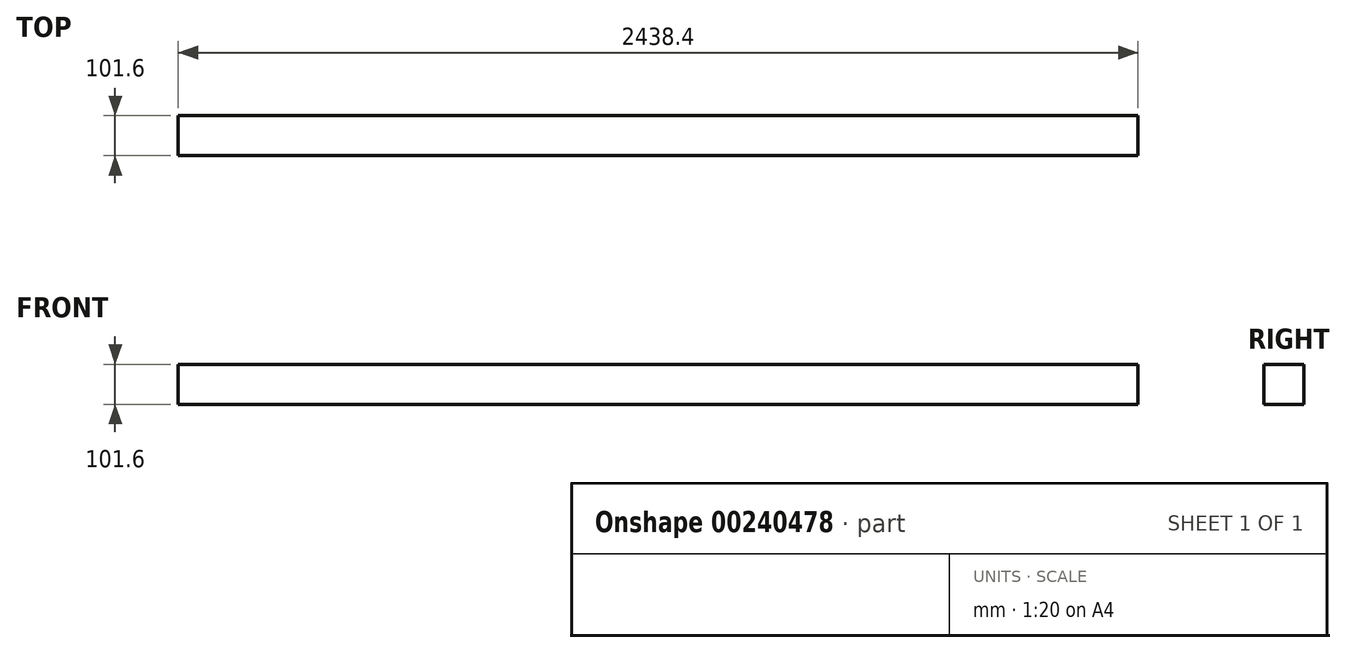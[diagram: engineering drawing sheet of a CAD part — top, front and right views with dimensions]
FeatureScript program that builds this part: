
annotation { "Feature Type Name" : "Feature", "Feature Type Description" : "" }
export const myFeature = defineFeature(function(context is Context, id is Id, definition is map)
    precondition{}
    {
        {
            var Q0;
            Q0=qCreatedBy(makeId("Right.planeOp"),FACE);
            var sketch = newSketch(context, id + "F0", { "sketchPlane" : qUnion([Q0])});
            skLineSegment(sketch, "E0.bottom", {"start": v(-22.92, 101.46) * mm, "end": v(78.68, 101.46) * mm});
            skLineSegment(sketch, "E0.top", {"start": v(-22.92, -0.14) * mm, "end": v(78.68, -0.14) * mm});
            skLineSegment(sketch, "E0.left", {"start": v(-22.92, 101.46) * mm, "end": v(-22.92, -0.14) * mm});
            skLineSegment(sketch, "E0.right", {"start": v(78.68, 101.46) * mm, "end": v(78.68, -0.14) * mm});
            skSolve(sketch);
        }
        {
            var Q0;
            Q0 = qSketchRegion(id + "F0", true);
            extrude(context, id + "F1", {"entities" : qUnion([Q0]), "depth" : 2438.4 * mm});
        }
    });
